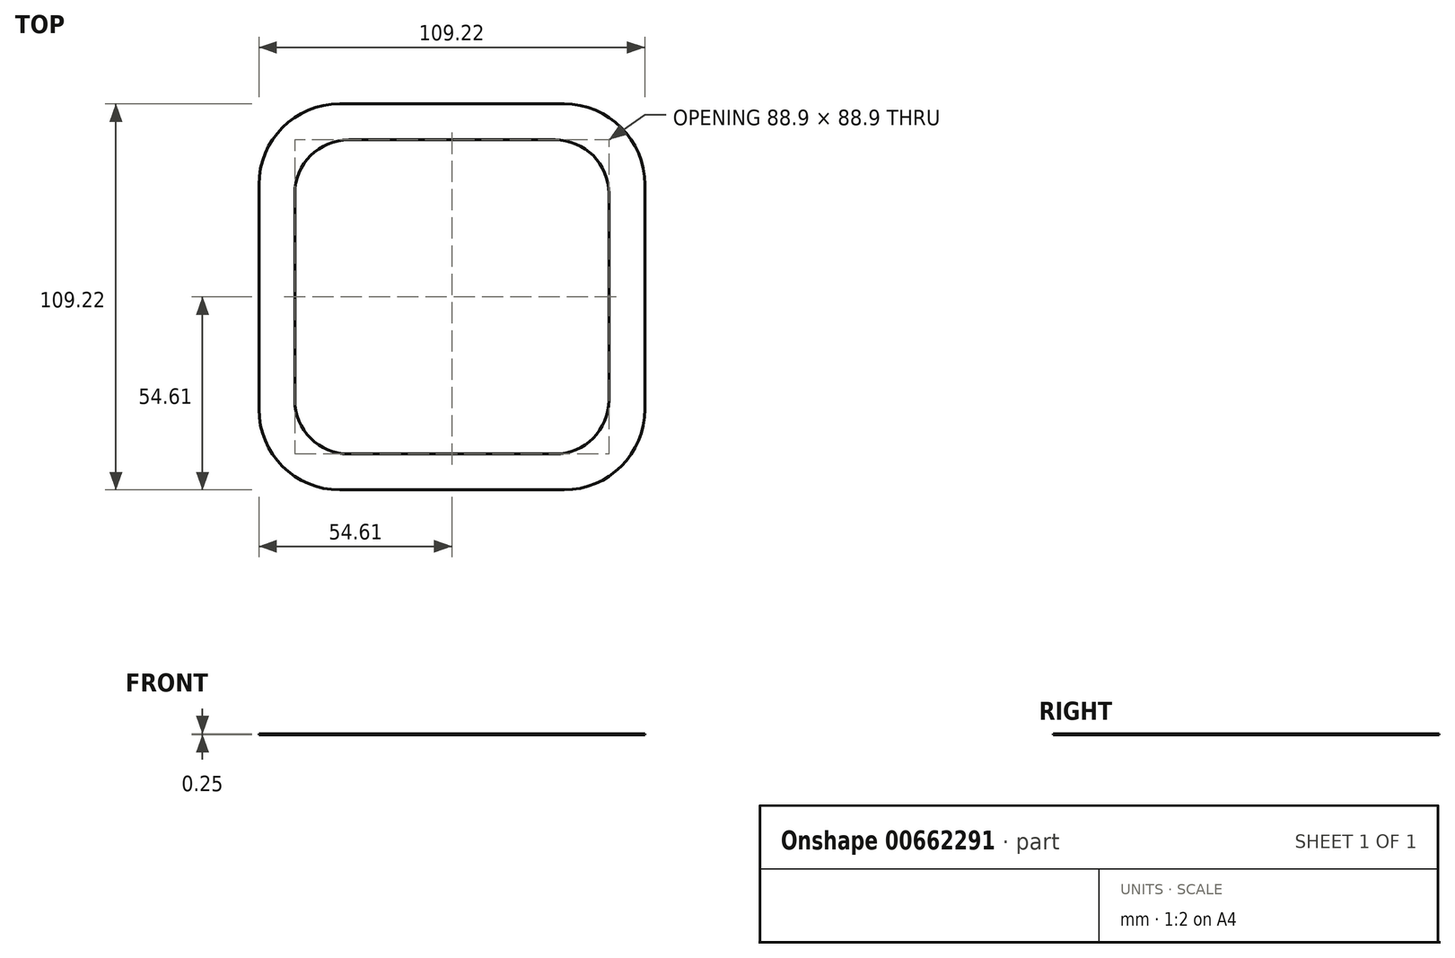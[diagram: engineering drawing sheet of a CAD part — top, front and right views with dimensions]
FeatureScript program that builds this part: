
annotation { "Feature Type Name" : "Feature", "Feature Type Description" : "" }
export const myFeature = defineFeature(function(context is Context, id is Id, definition is map)
    precondition{}
    {
        {
            var Q0;
            Q0=qCreatedBy(makeId("Top.planeOp"),FACE);
            var sketch = newSketch(context, id + "F0", { "sketchPlane" : qUnion([Q0])});
            skLineSegment(sketch, "E0.bottom", {"start": v(29.21, -44.45) * mm, "end": v(-29.21, -44.45) * mm});
            skLineSegment(sketch, "E0.top", {"start": v(29.21, 44.45) * mm, "end": v(-29.21, 44.45) * mm});
            skLineSegment(sketch, "E0.left", {"start": v(44.45, -29.21) * mm, "end": v(44.45, 29.21) * mm});
            skLineSegment(sketch, "E0.right", {"start": v(-44.45, -29.21) * mm, "end": v(-44.45, 29.21) * mm});
            skPoint(sketch, "E0.middle", {"position": v(0, 0) * mm});
            skPoint(sketch, "E1.visualSharp", {"position": v(-44.45, -44.45) * mm});
            skArc(sketch, "E1.filletArc", {"start": v(-44.45, -29.21) * mm, "mid": v(-39.99, -39.99) * mm, "end": v(-29.21, -44.45) * mm});
            skPoint(sketch, "E2.visualSharp", {"position": v(-44.45, 44.45) * mm});
            skArc(sketch, "E2.filletArc", {"start": v(-29.21, 44.45) * mm, "mid": v(-39.99, 39.99) * mm, "end": v(-44.45, 29.21) * mm});
            skPoint(sketch, "E3.visualSharp", {"position": v(44.45, 44.45) * mm});
            skArc(sketch, "E3.filletArc", {"start": v(44.45, 29.21) * mm, "mid": v(39.99, 39.99) * mm, "end": v(29.21, 44.45) * mm});
            skPoint(sketch, "E4.visualSharp", {"position": v(44.45, -44.45) * mm});
            skArc(sketch, "E4.filletArc", {"start": v(29.21, -44.45) * mm, "mid": v(39.99, -39.99) * mm, "end": v(44.45, -29.21) * mm});
            skLineSegment(sketch, "E5.bottom", {"start": v(31.75, -54.61) * mm, "end": v(-31.75, -54.61) * mm});
            skLineSegment(sketch, "E5.top", {"start": v(31.75, 54.61) * mm, "end": v(-31.75, 54.6) * mm});
            skLineSegment(sketch, "E5.left", {"start": v(54.61, -31.75) * mm, "end": v(54.61, 31.75) * mm});
            skLineSegment(sketch, "E5.right", {"start": v(-54.61, -31.75) * mm, "end": v(-54.61, 31.75) * mm});
            skPoint(sketch, "E6.visualSharp", {"position": v(-54.61, 54.6) * mm});
            skArc(sketch, "E6.filletArc", {"start": v(-31.75, 54.61) * mm, "mid": v(-47.91, 47.91) * mm, "end": v(-54.61, 31.75) * mm});
            skPoint(sketch, "E7.visualSharp", {"position": v(-54.61, -54.61) * mm});
            skArc(sketch, "E7.filletArc", {"start": v(-54.61, -31.75) * mm, "mid": v(-47.91, -47.91) * mm, "end": v(-31.75, -54.61) * mm});
            skPoint(sketch, "E8.visualSharp", {"position": v(54.6, -54.6) * mm});
            skArc(sketch, "E8.filletArc", {"start": v(31.75, -54.61) * mm, "mid": v(47.91, -47.91) * mm, "end": v(54.61, -31.75) * mm});
            skPoint(sketch, "E9.visualSharp", {"position": v(54.61, 54.61) * mm});
            skArc(sketch, "E9.filletArc", {"start": v(54.61, 31.75) * mm, "mid": v(47.91, 47.91) * mm, "end": v(31.75, 54.61) * mm});
            skSolve(sketch);
        }
        {
            var Q0;
            Q0=qSketchRegion(id+"F0",true);
            extrude(context, id + "F1", {"entities" : qUnion([Q0]), "depth" : 0.25 * mm});
        }
    });
